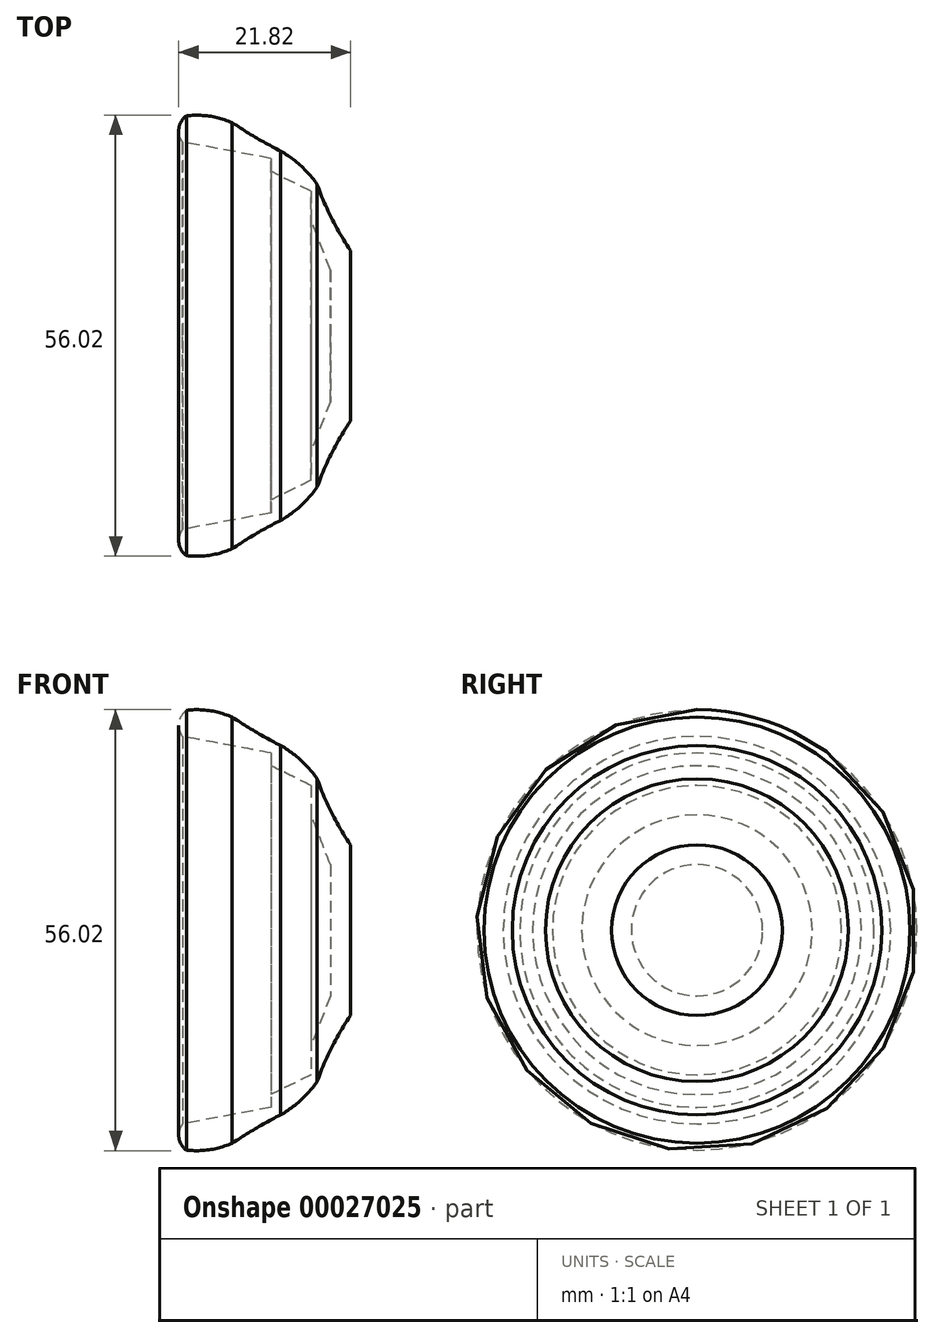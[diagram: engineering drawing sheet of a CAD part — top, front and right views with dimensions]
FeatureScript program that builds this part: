
annotation { "Feature Type Name" : "Feature", "Feature Type Description" : "" }
export const myFeature = defineFeature(function(context is Context, id is Id, definition is map)
    precondition{}
    {
        {
            var Q0;
            Q0=qCreatedBy(makeId("Front.planeOp"),FACE);
            var sketch = newSketch(context, id + "F0", { "sketchPlane" : qUnion([Q0])});
            skLineSegment(sketch, "E0", {"start": v(0, 0) * mm, "end": v(0, 10.84) * mm});
            skLineSegment(sketch, "E1", {"start": v(0, 10.84) * mm, "end": v(-4.23, 15.67) * mm});
            skLineSegment(sketch, "E2", {"start": v(-4.23, 15.67) * mm, "end": v(-4.23, 19.22) * mm});
            skLineSegment(sketch, "E3", {"start": v(-4.23, 19.22) * mm, "end": v(-8.88, 21.55) * mm});
            skLineSegment(sketch, "E4", {"start": v(-8.88, 21.55) * mm, "end": v(-8.88, 23.46) * mm});
            skLineSegment(sketch, "E5", {"start": v(-8.88, 23.46) * mm, "end": v(-15.02, 24.61) * mm});
            skLineSegment(sketch, "E6", {"start": v(-15.02, 24.61) * mm, "end": v(-15.02, 27.06) * mm});
            skLineSegment(sketch, "E7", {"start": v(-15.02, 27.06) * mm, "end": v(-20.83, 27.94) * mm});
            skLineSegment(sketch, "E8", {"start": v(-20.83, 27.94) * mm, "end": v(-21.34, 24.61) * mm});
            skLineSegment(sketch, "E9", {"start": v(-21.34, 24.61) * mm, "end": v(-10.1, 22.5) * mm});
            skLineSegment(sketch, "E10", {"start": v(-10.1, 22.5) * mm, "end": v(-10.1, 20.88) * mm});
            skLineSegment(sketch, "E11", {"start": v(-10.1, 20.88) * mm, "end": v(-5, 18.37) * mm});
            skLineSegment(sketch, "E12", {"start": v(-5, 18.37) * mm, "end": v(-5, 14.65) * mm});
            skLineSegment(sketch, "E13", {"start": v(-5, 14.65) * mm, "end": v(-2.55, 8.34) * mm});
            skLineSegment(sketch, "E14", {"start": v(-2.55, 8.34) * mm, "end": v(-2.55, 0) * mm});
            skLineSegment(sketch, "E15", {"start": v(-2.55, 0) * mm, "end": v(0, 0) * mm});
            skArc(sketch, "E16", {"start": v(-20.83, 27.94) * mm, "mid": v(-21.8, 26.38) * mm, "end": v(-21.34, 24.61) * mm});
            skArc(sketch, "E17", {"start": v(-15.02, 27.06) * mm, "mid": v(-17.87, 27.88) * mm, "end": v(-20.83, 27.94) * mm});
            skArc(sketch, "E18", {"start": v(-15.02, 27.06) * mm, "mid": v(-12, 25.16) * mm, "end": v(-8.88, 23.46) * mm});
            skArc(sketch, "E19", {"start": v(-4.23, 19.22) * mm, "mid": v(-6.32, 21.6) * mm, "end": v(-8.88, 23.46) * mm});
            skArc(sketch, "E20", {"start": v(-4.23, 19.22) * mm, "mid": v(-2.38, 14.9) * mm, "end": v(0, 10.84) * mm});
            skSolve(sketch);
        }
        {
            var Q0;
            Q0=makeQuery(id+"F0.imprint","IMPRINT",FACE,{"disambiguationData":[TD([[makeQuery(id+"F0.imprint","IMPRINT",EDGE,{"derivedFrom":sQuery(id+"F0.wireOp",EDGE,"E0")}),1.0]])]});
            var Q1;
            Q1=sQuery(id+"F0.wireOp",EDGE,"E15");
            revolve(context, id + "F1", {"entities" : qUnion([Q0]), "axis" : qUnion([Q1]), "revolveType" : RevolveType.FULL});
        }
        {
            var Q0;
            Q0 = qSketchRegion(id + "F0", true);
            var Q1;
            Q1=sQuery(id+"F0.wireOp",EDGE,"E15");
            revolve(context, id + "F2", {"operationType" : NewBodyOperationType.ADD, "entities" : qUnion([Q0]), "axis" : qUnion([Q1]), "revolveType" : RevolveType.FULL});
        }
    });
